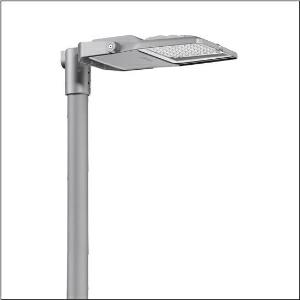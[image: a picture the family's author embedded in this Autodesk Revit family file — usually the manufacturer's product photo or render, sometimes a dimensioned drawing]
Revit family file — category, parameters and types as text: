
# Revit family: floodlight_fl_21_mini___pl33t_5xa7776c2f3a_ca81
name_source: partatom
category: Lighting Fixtures
units: mm (PartAtom-declared; Revit-internal decimal feet)

## family parameters
Cut with Voids When Loaded = No
Host = Face
Light Source = No
Part Type = Normal
Room Calculation Point = No
Round Connector Dimension = Use Diameter
Shared = No

## types (1)
- --- (1 x LED, 12050 lm, 89 W, 3000K)
    Apparent Load = 89 VA
    CIE Flux Codes = 26 75 99 100 100
    Color Rendering = 70
    Color Temperature = 3000K
    Default Elevation = 1800 mm
    Description = Floodlight FL 21 mini, floodlight, primary light control with lens, of PMMA, primary optical cover: protective disc, of toughened safety glass, transparent, light distribution: PL33T, light emission: direct distribution, installation type: surface-mounted, LED, High Power LED, rated luminous flux: 12.050lm, luminous efficacy: 135lm/W, light colour: 730, colour temperature: 3000K, control: flexible luminous flux parameterisation, time-dependent luminous flux control, constant luminous flux control, overheat protection, pre-setting: logarithmic dimming characteristic, with terminal, 6-pole, mains connection: 220..240V, AC, 50/60Hz, start of lifetime: 89W, end of service life: 94W, reduction: 43W, luminaire housing, of diecast aluminium, powder-coated, Siteco® metallic grey (DB 702S), corrosivity category C5 mid according to DIN EN ISO 12944, sealing non-destructively replaceable, please order mast flange separately, mast bracket, of steel, galvanised, powder-coated, Siteco® metallic grey (DB 702S), Smart Interface below and above, protection rating (complete): IP66, insulation class (complete): insulation class II (safety insulation), certification: CE, ENEC, VDE, protection symbol: D, impact resistance: IK08, permissible operating ambient temperature: -40..+40°C, permissible operating ambient temperature for outdoor applications: -40..+50°C, standard: DIN EN 12944, LABS conformity tested according to VDMA 24364:2018-05, packaging unit: 1 piece

Light Distribution: PL33T
    Height = 70 mm
    Lamp = 1 x LED
    Lamp Light Flux = 12050 lm
    Lamp Power = 89 W
    Lamp count = 1
    Length = 485 mm
    Luminous efficacy = 135 lm/W
    Manufacturer = Siteco
    ModVariant = No
    Model = 5XA7776C2F3A
    Number of Poles = 1
    OnlyDefault = Yes
    Power Factor = 1
    Product Name = Floodlight FL 21 mini | PL33T
    Product group = floodlight | pylon annexe
    ProductGroupID = 6200
    Protection Class = Protection class II
    Protection Degree = IP 66
    RLX_Detail_Level = 1
    RLX_Emergency_Light_Flux = 0 lm
    RLX_Emergency_Type = 0
    RLX_Emergency_Type_DB = No
    RlxData = <blob elided: 100813 chars, md5=67e25ba5>
    Socket = socket
    Standby Power = 0 W
    System Light Flux = 12050 lm
    System Power = 89 W
    Type Comments = factory setting: luminous flux: 100 % | dim-lin: 254 | 456 mA
    Type Image = l_1007125.jpg
    URL = http://relux.com
    VarID = @adj_118811
    Voltage = 0 V
    Weight = 0.00 kg
    Width = 337 mm

## geometry (parser evidence)
native form markers: Blend x4, Sweep x14
no freeform markers — native parametric forms only
